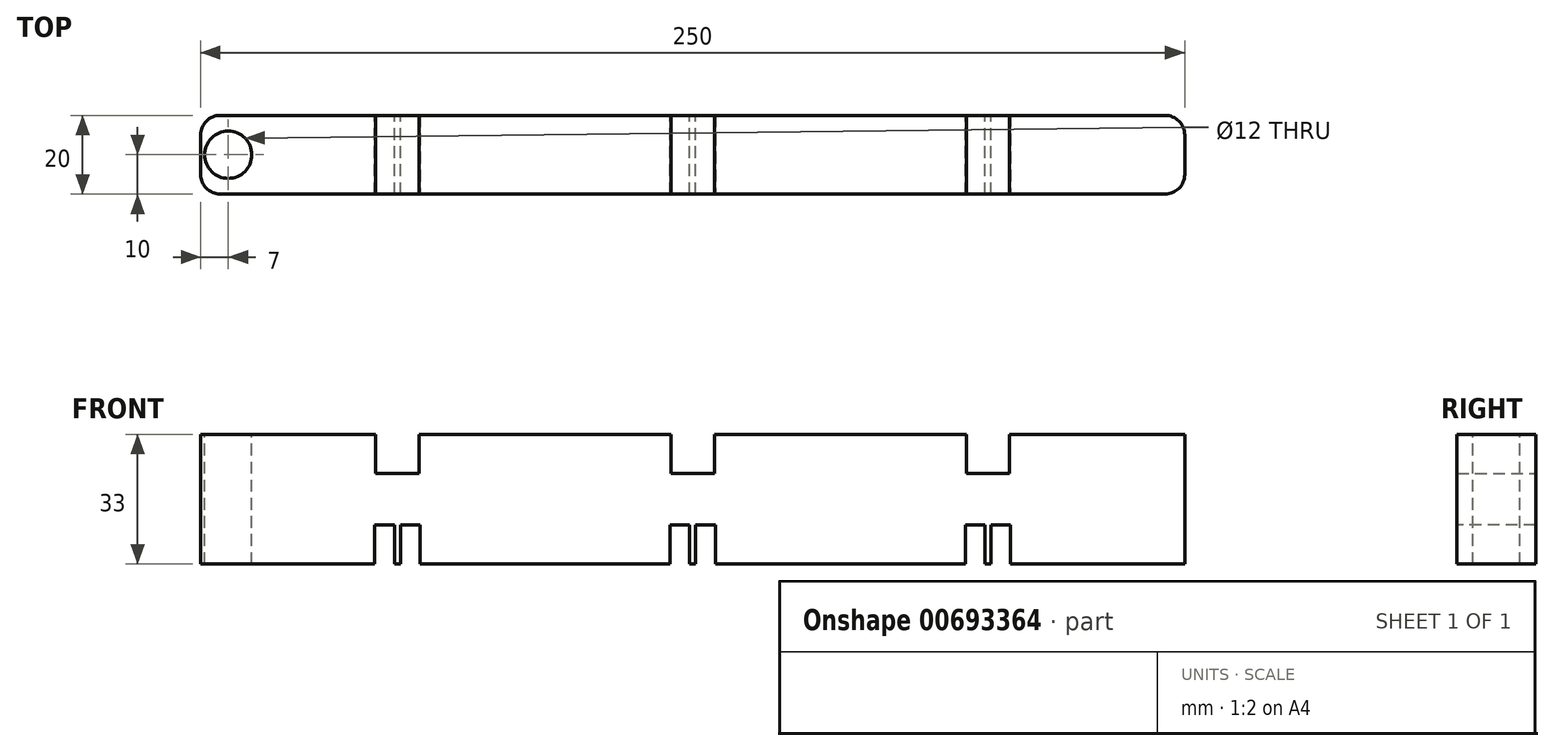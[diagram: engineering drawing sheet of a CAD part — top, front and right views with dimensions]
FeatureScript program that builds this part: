
annotation { "Feature Type Name" : "Feature", "Feature Type Description" : "" }
export const myFeature = defineFeature(function(context is Context, id is Id, definition is map)
    precondition{}
    {
        {
            var Q0;
            Q0=qCreatedBy(makeId("Front.planeOp"),FACE);
            var sketch = newSketch(context, id + "F0", { "sketchPlane" : qUnion([Q0])});
            skLineSegment(sketch, "E0.0", {"start": v(-125, 16.5) * mm, "end": v(125, 16.5) * mm});
            skLineSegment(sketch, "E0.1", {"start": v(125, 16.5) * mm, "end": v(125, -16.5) * mm});
            skLineSegment(sketch, "E0.2", {"start": v(125, -16.5) * mm, "end": v(-125, -16.5) * mm});
            skLineSegment(sketch, "E0.3", {"start": v(-125, -16.5) * mm, "end": v(-125, 16.5) * mm});
            skPoint(sketch, "E0.0.midPoint", {"position": v(0, 16.5) * mm});
            skLineSegment(sketch, "E1", {"start": v(-125, 0) * mm, "end": v(125, 0) * mm, "construction": true});
            skPoint(sketch, "E2", {"position": v(0, 0) * mm});
            skSolve(sketch);
        }
        {
            var Q0;
            Q0=makeQuery(id+"F0.imprint","IMPRINT",FACE,{"disambiguationData":[TD([[makeQuery(id+"F0.imprint","IMPRINT",EDGE,{"derivedFrom":sQuery(id+"F0.wireOp",EDGE,"E0.0")}),-1.0]])]});
            extrude(context, id + "F1", {"entities" : qUnion([Q0]), "depth" : 20 * mm, "offsetDistance" : 25 * mm});
        }
        {
            var Q0;
            Q0=makeQuery(id+"F1.opExtrude","SWEPT_FACE",FACE,{"disambiguationData":[OSD([sQuery(id+"F0.wireOp",EDGE,"E0.0")])]});
            var sketch = newSketch(context, id + "F2", { "sketchPlane" : qUnion([Q0])});
            skLineSegment(sketch, "E3", {"start": v(5.5, 0) * mm, "end": v(5.5, -20) * mm});
            skLineSegment(sketch, "E4", {"start": v(-5.5, -20) * mm, "end": v(5.5, -20) * mm});
            skLineSegment(sketch, "E5", {"start": v(-5.5, -20) * mm, "end": v(-5.5, 0) * mm});
            skLineSegment(sketch, "E6", {"start": v(5.5, 0) * mm, "end": v(-5.5, 0) * mm});
            skLineSegment(sketch, "E7", {"start": v(0, 0) * mm, "end": v(0, -20) * mm, "construction": true});
            skLineSegment(sketch, "E8", {"start": v(-125, -10) * mm, "end": v(125, -10) * mm, "construction": true});
            skPoint(sketch, "E9", {"position": v(0, -10) * mm});
            skPoint(sketch, "E10.1.0.0", {"position": v(75, -10) * mm});
            skLineSegment(sketch, "E10.1.0.1", {"start": v(69.5, -20) * mm, "end": v(69.5, 0) * mm});
            skLineSegment(sketch, "E10.1.0.2", {"start": v(69.5, -20) * mm, "end": v(80.5, -20) * mm});
            skLineSegment(sketch, "E10.1.0.3", {"start": v(80.5, 0) * mm, "end": v(80.5, -20) * mm});
            skLineSegment(sketch, "E10.1.0.4", {"start": v(80.5, 0) * mm, "end": v(69.5, 0) * mm});
            skLineSegment(sketch, "E10.1.0.5", {"start": v(75, 0) * mm, "end": v(75, -20) * mm, "construction": true});
            skLineSegment(sketch, "E10.direction1", {"start": v(-5.5, -20) * mm, "end": v(69.5, -20) * mm, "construction": true});
            skPoint(sketch, "E11.1.0.0", {"position": v(-75, -10) * mm});
            skLineSegment(sketch, "E11.1.0.1", {"start": v(-69.5, 0) * mm, "end": v(-69.5, -20) * mm});
            skLineSegment(sketch, "E11.1.0.2", {"start": v(-80.5, -20) * mm, "end": v(-69.5, -20) * mm});
            skLineSegment(sketch, "E11.1.0.3", {"start": v(-80.5, -20) * mm, "end": v(-80.5, 0) * mm});
            skLineSegment(sketch, "E11.1.0.4", {"start": v(-69.5, 0) * mm, "end": v(-80.5, 0) * mm});
            skLineSegment(sketch, "E11.1.0.5", {"start": v(-75, 0) * mm, "end": v(-75, -20) * mm, "construction": true});
            skLineSegment(sketch, "E11.direction1", {"start": v(-5.5, -20) * mm, "end": v(-80.5, -20) * mm, "construction": true});
            skSolve(sketch);
        }
        {
            var Q0;
            Q0=makeQuery(id+"F1.opExtrude","SWEPT_FACE",FACE,{"disambiguationData":[OSD([sQuery(id+"F0.wireOp",EDGE,"E0.2")])]});
            var sketch = newSketch(context, id + "F3", { "sketchPlane" : qUnion([Q0])});
            skLineSegment(sketch, "E12.bottom", {"start": v(-5.75, 20) * mm, "end": v(-0.75, 20) * mm});
            skLineSegment(sketch, "E12.top", {"start": v(-5.75, 0) * mm, "end": v(-0.75, 0) * mm});
            skLineSegment(sketch, "E12.left", {"start": v(-5.75, 20) * mm, "end": v(-5.75, 0) * mm});
            skLineSegment(sketch, "E12.right", {"start": v(-0.75, 20) * mm, "end": v(-0.75, 0) * mm});
            skLineSegment(sketch, "E13", {"start": v(0.75, 20) * mm, "end": v(0.75, 0) * mm});
            skLineSegment(sketch, "E14", {"start": v(0.75, 0) * mm, "end": v(5.75, 0) * mm});
            skLineSegment(sketch, "E15", {"start": v(5.75, 0) * mm, "end": v(5.75, 20) * mm});
            skLineSegment(sketch, "E16", {"start": v(5.75, 20) * mm, "end": v(0.75, 20) * mm});
            skLineSegment(sketch, "E17", {"start": v(-0.75, 10) * mm, "end": v(0.75, 10) * mm, "construction": true});
            skPoint(sketch, "E18", {"position": v(0, 10) * mm});
            skLineSegment(sketch, "E19.1.0.0", {"start": v(80.75, 0) * mm, "end": v(80.75, 20) * mm});
            skLineSegment(sketch, "E19.1.0.1", {"start": v(75.75, 20) * mm, "end": v(75.75, 0) * mm});
            skLineSegment(sketch, "E19.1.0.2", {"start": v(69.25, 0) * mm, "end": v(74.25, 0) * mm});
            skPoint(sketch, "E19.1.0.3", {"position": v(75, 10) * mm});
            skLineSegment(sketch, "E19.1.0.4", {"start": v(69.25, 20) * mm, "end": v(74.25, 20) * mm});
            skLineSegment(sketch, "E19.1.0.5", {"start": v(75.75, 0) * mm, "end": v(80.75, 0) * mm});
            skLineSegment(sketch, "E19.1.0.6", {"start": v(74.25, 20) * mm, "end": v(74.25, 0) * mm});
            skLineSegment(sketch, "E19.1.0.7", {"start": v(69.25, 20) * mm, "end": v(69.25, 0) * mm});
            skLineSegment(sketch, "E19.1.0.8", {"start": v(80.75, 20) * mm, "end": v(75.75, 20) * mm});
            skLineSegment(sketch, "E19.1.0.9", {"start": v(74.25, 10) * mm, "end": v(75.75, 10) * mm, "construction": true});
            skLineSegment(sketch, "E19.direction1", {"start": v(-5.75, 0) * mm, "end": v(69.25, 0) * mm, "construction": true});
            skLineSegment(sketch, "E20.1.0.0", {"start": v(-80.75, 20) * mm, "end": v(-75.75, 20) * mm});
            skPoint(sketch, "E20.1.0.1", {"position": v(-75, 10) * mm});
            skLineSegment(sketch, "E20.1.0.2", {"start": v(-80.75, 0) * mm, "end": v(-75.75, 0) * mm});
            skLineSegment(sketch, "E20.1.0.3", {"start": v(-80.75, 20) * mm, "end": v(-80.75, 0) * mm});
            skLineSegment(sketch, "E20.1.0.4", {"start": v(-75.75, 20) * mm, "end": v(-75.75, 0) * mm});
            skLineSegment(sketch, "E20.1.0.5", {"start": v(-74.25, 20) * mm, "end": v(-74.25, 0) * mm});
            skLineSegment(sketch, "E20.1.0.6", {"start": v(-74.25, 0) * mm, "end": v(-69.25, 0) * mm});
            skLineSegment(sketch, "E20.1.0.7", {"start": v(-69.25, 0) * mm, "end": v(-69.25, 20) * mm});
            skLineSegment(sketch, "E20.1.0.8", {"start": v(-69.25, 20) * mm, "end": v(-74.25, 20) * mm});
            skLineSegment(sketch, "E20.1.0.9", {"start": v(-75.75, 10) * mm, "end": v(-74.25, 10) * mm, "construction": true});
            skLineSegment(sketch, "E20.direction1", {"start": v(-5.75, 0) * mm, "end": v(-80.75, 0) * mm, "construction": true});
            skSolve(sketch);
        }
        {
            var Q0;
            Q0=makeQuery(id+"F2.imprint","IMPRINT",FACE,{"disambiguationData":[TD([[makeQuery(id+"F2.imprint","IMPRINT",EDGE,{"derivedFrom":sQuery(id+"F2.wireOp",EDGE,"E11.1.0.1")}),-1.0]])]});
            var Q1;
            Q1=makeQuery(id+"F2.imprint","IMPRINT",FACE,{"disambiguationData":[TD([[makeQuery(id+"F2.imprint","IMPRINT",EDGE,{"derivedFrom":sQuery(id+"F2.wireOp",EDGE,"E3")}),-1.0]])]});
            var Q2;
            Q2=makeQuery(id+"F2.imprint","IMPRINT",FACE,{"disambiguationData":[TD([[makeQuery(id+"F2.imprint","IMPRINT",EDGE,{"derivedFrom":sQuery(id+"F2.wireOp",EDGE,"E10.1.0.1")}),-1.0]])]});
            extrude(context, id + "F4", {"entities" : qUnion([Q0, Q1, Q2]), "operationType" : NewBodyOperationType.REMOVE, "oppositeDirection" : true, "depth" : 10 * mm, "offsetDistance" : 25 * mm});
        }
        {
            var Q0;
            Q0=makeQuery(id+"F3.imprint","IMPRINT",FACE,{"disambiguationData":[TD([[makeQuery(id+"F3.imprint","IMPRINT",EDGE,{"derivedFrom":sQuery(id+"F3.wireOp",EDGE,"E20.1.0.0")}),1.0]])]});
            var Q1;
            Q1=makeQuery(id+"F3.imprint","IMPRINT",FACE,{"disambiguationData":[TD([[makeQuery(id+"F3.imprint","IMPRINT",EDGE,{"derivedFrom":sQuery(id+"F3.wireOp",EDGE,"E20.1.0.5")}),1.0]])]});
            var Q2;
            Q2=makeQuery(id+"F3.imprint","IMPRINT",FACE,{"disambiguationData":[TD([[makeQuery(id+"F3.imprint","IMPRINT",EDGE,{"derivedFrom":sQuery(id+"F3.wireOp",EDGE,"E12.bottom")}),1.0]])]});
            var Q3;
            Q3=makeQuery(id+"F3.imprint","IMPRINT",FACE,{"disambiguationData":[TD([[makeQuery(id+"F3.imprint","IMPRINT",EDGE,{"derivedFrom":sQuery(id+"F3.wireOp",EDGE,"E13")}),1.0]])]});
            var Q4;
            Q4=makeQuery(id+"F3.imprint","IMPRINT",FACE,{"disambiguationData":[TD([[makeQuery(id+"F3.imprint","IMPRINT",EDGE,{"derivedFrom":sQuery(id+"F3.wireOp",EDGE,"E19.1.0.2")}),-1.0]])]});
            var Q5;
            Q5=makeQuery(id+"F3.imprint","IMPRINT",FACE,{"disambiguationData":[TD([[makeQuery(id+"F3.imprint","IMPRINT",EDGE,{"derivedFrom":sQuery(id+"F3.wireOp",EDGE,"E19.1.0.0")}),1.0]])]});
            extrude(context, id + "F5", {"entities" : qUnion([Q0, Q1, Q2, Q3, Q4, Q5]), "operationType" : NewBodyOperationType.REMOVE, "oppositeDirection" : true, "depth" : 10 * mm, "offsetDistance" : 25 * mm});
        }
        {
            var Q0;
            Q0=makeQuery(id+"F1.opExtrude","CAP_EDGE",EDGE,{"disambiguationData":[OSD([sQuery(id+"F0.wireOp",EDGE,"E0.3")])],"isStart":false});
            fillet(context, id + "F6", {"entities" : qUnion([Q0]), "radius" : 5 * mm, "tangentPropagation" : true, "allowEdgeOverflow" : false});
        }
        {
            var Q0;
            Q0=makeQuery(id+"F1.opExtrude","CAP_EDGE",EDGE,{"disambiguationData":[OSD([sQuery(id+"F0.wireOp",EDGE,"E0.3")])],"isStart":true});
            fillet(context, id + "F7", {"entities" : qUnion([Q0]), "radius" : 5 * mm, "tangentPropagation" : true, "allowEdgeOverflow" : false});
        }
        {
            var Q0;
            Q0=makeQuery(id+"F1.opExtrude","CAP_EDGE",EDGE,{"disambiguationData":[OSD([sQuery(id+"F0.wireOp",EDGE,"E0.1")])],"isStart":false});
            fillet(context, id + "F8", {"entities" : qUnion([Q0]), "radius" : 5 * mm, "tangentPropagation" : true, "allowEdgeOverflow" : false});
        }
        {
            var Q0;
            Q0=makeQuery(id+"F1.opExtrude","CAP_EDGE",EDGE,{"disambiguationData":[OSD([sQuery(id+"F0.wireOp",EDGE,"E0.1")])],"isStart":true});
            fillet(context, id + "F9", {"entities" : qUnion([Q0]), "radius" : 5 * mm, "tangentPropagation" : true, "allowEdgeOverflow" : false});
        }
        {
            var Q0;
            {var subQ0=sQuery(id+"F0.wireOp",EDGE,"E0.3");var subQ3=sQuery(id+"F0.wireOp",EDGE,"E0.0");Q0=makeQuery(id+"F4.boolean.opBoolean","SPLIT",FACE,{"disambiguationData":[TD([makeQuery(id+"F1.opExtrude","SWEPT_FACE",FACE,{"disambiguationData":[OSD([subQ0])]})])],"derivedFrom":makeQuery(id+"F1.opExtrude","SWEPT_FACE",FACE,{"disambiguationData":[OSD([subQ3])]})});}
            var sketch = newSketch(context, id + "F10", { "sketchPlane" : qUnion([Q0])});
            skCircle(sketch, "E21", {"center": v(-118, -10) * mm, "radius": 6 * mm});
            skPoint(sketch, "E21.centerSnap0", {"position": v(-125, -10) * mm});
            skPoint(sketch, "E22.centerSnap0", {"position": v(-80.5, -10) * mm});
            skCircle(sketch, "E23.MirrorC", {"center": v(118, -10) * mm, "radius": 6 * mm});
            skSolve(sketch);
        }
        {
            var Q0;
            Q0=makeQuery(id+"F10.imprint","IMPRINT",FACE,{"disambiguationData":[TD([[makeQuery(id+"F10.imprint","IMPRINT",EDGE,{"derivedFrom":sQuery(id+"F10.wireOp",EDGE,"E23.MirrorC")}),-1.0]])]});
            var Q1;
            Q1=makeQuery(id+"F10.imprint","IMPRINT",FACE,{"disambiguationData":[TD([[makeQuery(id+"F10.imprint","IMPRINT",EDGE,{"derivedFrom":sQuery(id+"F10.wireOp",EDGE,"E21")}),1.0]])]});
            extrude(context, id + "F11", {"entities" : qUnion([Q0, Q1]), "operationType" : NewBodyOperationType.REMOVE, "endBound" : BoundingType.THROUGH_ALL, "oppositeDirection" : true, "depth" : 25 * mm, "offsetDistance" : 25 * mm});
        }
    });
